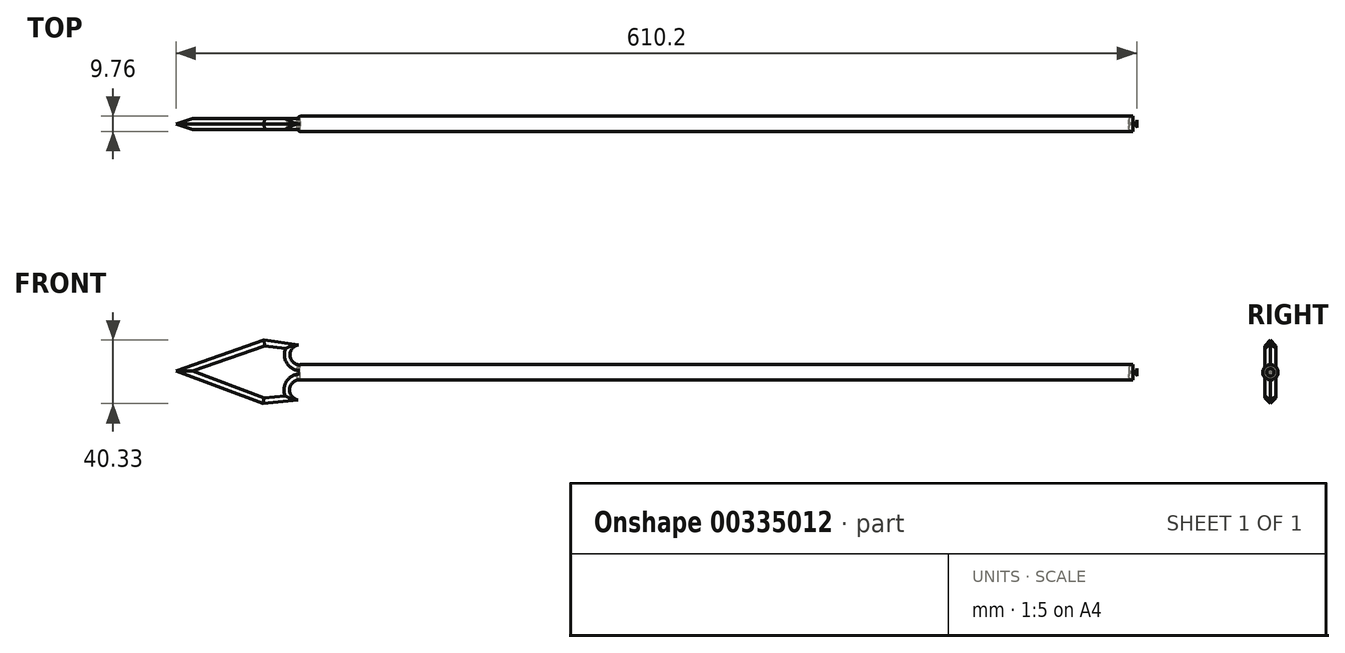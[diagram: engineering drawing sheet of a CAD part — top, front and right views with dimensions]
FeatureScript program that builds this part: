
annotation { "Feature Type Name" : "Feature", "Feature Type Description" : "" }
export const myFeature = defineFeature(function(context is Context, id is Id, definition is map)
    precondition{}
    {
        {
            var Q0;
            Q0=qCreatedBy(makeId("Front.planeOp"),FACE);
            var sketch = newSketch(context, id + "F0", { "sketchPlane" : qUnion([Q0])});
            skLineSegment(sketch, "E0.bottom", {"start": v(-146.96, 13.84) * mm, "end": v(386.44, 13.84) * mm});
            skLineSegment(sketch, "E0.top", {"start": v(-146.96, 8.96) * mm, "end": v(386.44, 8.96) * mm});
            skLineSegment(sketch, "E0.left", {"start": v(-146.96, 13.84) * mm, "end": v(-146.96, 8.96) * mm});
            skLineSegment(sketch, "E0.right", {"start": v(386.44, 13.84) * mm, "end": v(386.44, 8.96) * mm});
            skSolve(sketch);
        }
        {
            var Q0;
            Q0 = qSketchRegion(id + "F0", true);
            var Q1;
            Q1=sQuery(id+"F0.wireOp",EDGE,"E0.bottom");
            revolve(context, id + "F1", {"entities" : qUnion([Q0]), "axis" : qUnion([Q1]), "revolveType" : RevolveType.FULL});
        }
        {
            var Q0;
            Q0=qCreatedBy(makeId("Front.planeOp"),FACE);
            var sketch = newSketch(context, id + "F2", { "sketchPlane" : qUnion([Q0])});
            skArc(sketch, "E1", {"start": v(-145.23, 9.1) * mm, "mid": v(-151.64, 3.19) * mm, "end": v(-146.33, -3.73) * mm});
            skLineSegment(sketch, "E2", {"start": v(-224.66, 15.1) * mm, "end": v(-168.39, -6.1) * mm});
            skLineSegment(sketch, "E3", {"start": v(-168.39, -6.1) * mm, "end": v(-146.33, -3.73) * mm});
            skLineSegment(sketch, "E4", {"start": v(-145.23, 18.46) * mm, "end": v(-145.23, 9.1) * mm});
            skLineSegment(sketch, "E5", {"start": v(-145.23, 13.78) * mm, "end": v(-250.8, 15.1) * mm, "construction": true});
            skLineSegment(sketch, "E6.MirrorCS", {"start": v(-224.67, 14.44) * mm, "end": v(-167.88, 34.23) * mm});
            skLineSegment(sketch, "E7.MirrorCS", {"start": v(-167.88, 34.23) * mm, "end": v(-145.9, 31.3) * mm});
            skArc(sketch, "E8.MirrorCS", {"start": v(-145.1, 18.46) * mm, "mid": v(-151.38, 24.52) * mm, "end": v(-145.9, 31.3) * mm});
            skLineSegment(sketch, "E9.MirrorCS", {"start": v(-145.34, 9.1) * mm, "end": v(-145.1, 18.46) * mm});
            skSolve(sketch);
        }
        {
            var Q0;
            Q0=makeQuery(id+"F1.opRevolve","SWEPT_EDGE",EDGE,{"disambiguationData":[OSD([sQuery(id+"F0.wireOp",EDGE,"E0.top"),sQuery(id+"F0.wireOp",EDGE,"E0.right")])]});
            fillet(context, id + "F3", {"entities" : qUnion([Q0]), "radius" : 2.54 * mm, "tangentPropagation" : true, "allowEdgeOverflow" : false});
        }
        {
            var Q0;
            Q0 = qSketchRegion(id + "F2", true);
            extrude(context, id + "F4", {"entities" : qUnion([Q0]), "endBound" : BoundingType.SYMMETRIC, "depth" : 7.11 * mm});
        }
        {
            var Q0;
            Q0=makeQuery(id+"F4.opExtrude","CAP_EDGE",EDGE,{"disambiguationData":[OSD([sQuery(id+"F2.wireOp",EDGE,"E3")])],"isStart":true});
            var Q1;
            Q1=makeQuery(id+"F4.opExtrude","CAP_EDGE",EDGE,{"disambiguationData":[OSD([sQuery(id+"F2.wireOp",EDGE,"E2")])],"isStart":true});
            var Q2;
            Q2=makeQuery(id+"F4.opExtrude","CAP_EDGE",EDGE,{"disambiguationData":[OSD([sQuery(id+"F2.wireOp",EDGE,"E3")])],"isStart":false});
            var Q3;
            Q3=makeQuery(id+"F4.opExtrude","CAP_EDGE",EDGE,{"disambiguationData":[OSD([sQuery(id+"F2.wireOp",EDGE,"E2")])],"isStart":false});
            var Q4;
            Q4=makeQuery(id+"F4.opExtrude","CAP_EDGE",EDGE,{"disambiguationData":[OSD([sQuery(id+"F2.wireOp",EDGE,"CLEFTxV7-1z23-4vv7-0Sap-EByk14mVQZ6W")])],"isStart":false});
            var Q5;
            Q5=makeQuery(id+"F4.opExtrude","CAP_EDGE",EDGE,{"disambiguationData":[OSD([sQuery(id+"F2.wireOp",EDGE,"CLEFTxV7-1z23-4vv7-0Sap-EByk14mVQZ6W")])],"isStart":true});
            var Q6;
            Q6=makeQuery(id+"F4.opExtrude","CAP_EDGE",EDGE,{"disambiguationData":[OSD([sQuery(id+"F2.wireOp",EDGE,"DpLMorR3-N9C3-HqTt-RDwf-Cf340l360odD")])],"isStart":false});
            var Q7;
            Q7=makeQuery(id+"F4.opExtrude","CAP_EDGE",EDGE,{"disambiguationData":[OSD([sQuery(id+"F2.wireOp",EDGE,"6dQCvUv8-ExF1-p5Vb-hXI7-tNtqN0yIMqsn")])],"isStart":false});
            var Q8;
            Q8=makeQuery(id+"F4.opExtrude","CAP_EDGE",EDGE,{"disambiguationData":[OSD([sQuery(id+"F2.wireOp",EDGE,"E1")])],"isStart":false});
            var Q9;
            Q9=makeQuery(id+"F4.opExtrude","CAP_EDGE",EDGE,{"disambiguationData":[OSD([sQuery(id+"F2.wireOp",EDGE,"DpLMorR3-N9C3-HqTt-RDwf-Cf340l360odD")])],"isStart":true});
            var Q10;
            Q10=makeQuery(id+"F4.opExtrude","CAP_EDGE",EDGE,{"disambiguationData":[OSD([sQuery(id+"F2.wireOp",EDGE,"E1")])],"isStart":true});
            var Q11;
            Q11=makeQuery(id+"F4.opExtrude","CAP_EDGE",EDGE,{"disambiguationData":[OSD([sQuery(id+"F2.wireOp",EDGE,"6dQCvUv8-ExF1-p5Vb-hXI7-tNtqN0yIMqsn")])],"isStart":true});
            var Q12;
            Q12=makeQuery(id+"F4.opExtrude","CAP_EDGE",EDGE,{"disambiguationData":[OSD([sQuery(id+"F2.wireOp",EDGE,"E8.MirrorCS")])],"isStart":false});
            var Q13;
            Q13=makeQuery(id+"F4.opExtrude","CAP_EDGE",EDGE,{"disambiguationData":[OSD([sQuery(id+"F2.wireOp",EDGE,"E7.MirrorCS")])],"isStart":false});
            var Q14;
            Q14=makeQuery(id+"F4.opExtrude","CAP_EDGE",EDGE,{"disambiguationData":[OSD([sQuery(id+"F2.wireOp",EDGE,"E6.MirrorCS")])],"isStart":false});
            var Q15;
            Q15=makeQuery(id+"F4.opExtrude","CAP_EDGE",EDGE,{"disambiguationData":[OSD([sQuery(id+"F2.wireOp",EDGE,"E8.MirrorCS")])],"isStart":true});
            var Q16;
            Q16=makeQuery(id+"F4.opExtrude","CAP_EDGE",EDGE,{"disambiguationData":[OSD([sQuery(id+"F2.wireOp",EDGE,"E6.MirrorCS")])],"isStart":true});
            var Q17;
            Q17=makeQuery(id+"F4.opExtrude","CAP_EDGE",EDGE,{"disambiguationData":[OSD([sQuery(id+"F2.wireOp",EDGE,"E7.MirrorCS")])],"isStart":true});
            chamfer(context, id + "F5", {"entities" : qUnion([Q0, Q1, Q2, Q3, Q4, Q5, Q6, Q7, Q8, Q9, Q10, Q11, Q12, Q13, Q14, Q15, Q16, Q17]), "width" : 3.56 * mm, "tangentPropagation" : true});
        }
        {
            var Q0;
            Q0=makeQuery(id+"F1.opRevolve","SWEPT_EDGE",EDGE,{"disambiguationData":[OSD([sQuery(id+"F0.wireOp",EDGE,"E0.top"),sQuery(id+"F0.wireOp",EDGE,"E0.left")])]});
            fillet(context, id + "F6", {"entities" : qUnion([Q0]), "radius" : 2.54 * mm, "tangentPropagation" : true, "allowEdgeOverflow" : false});
        }
    });
